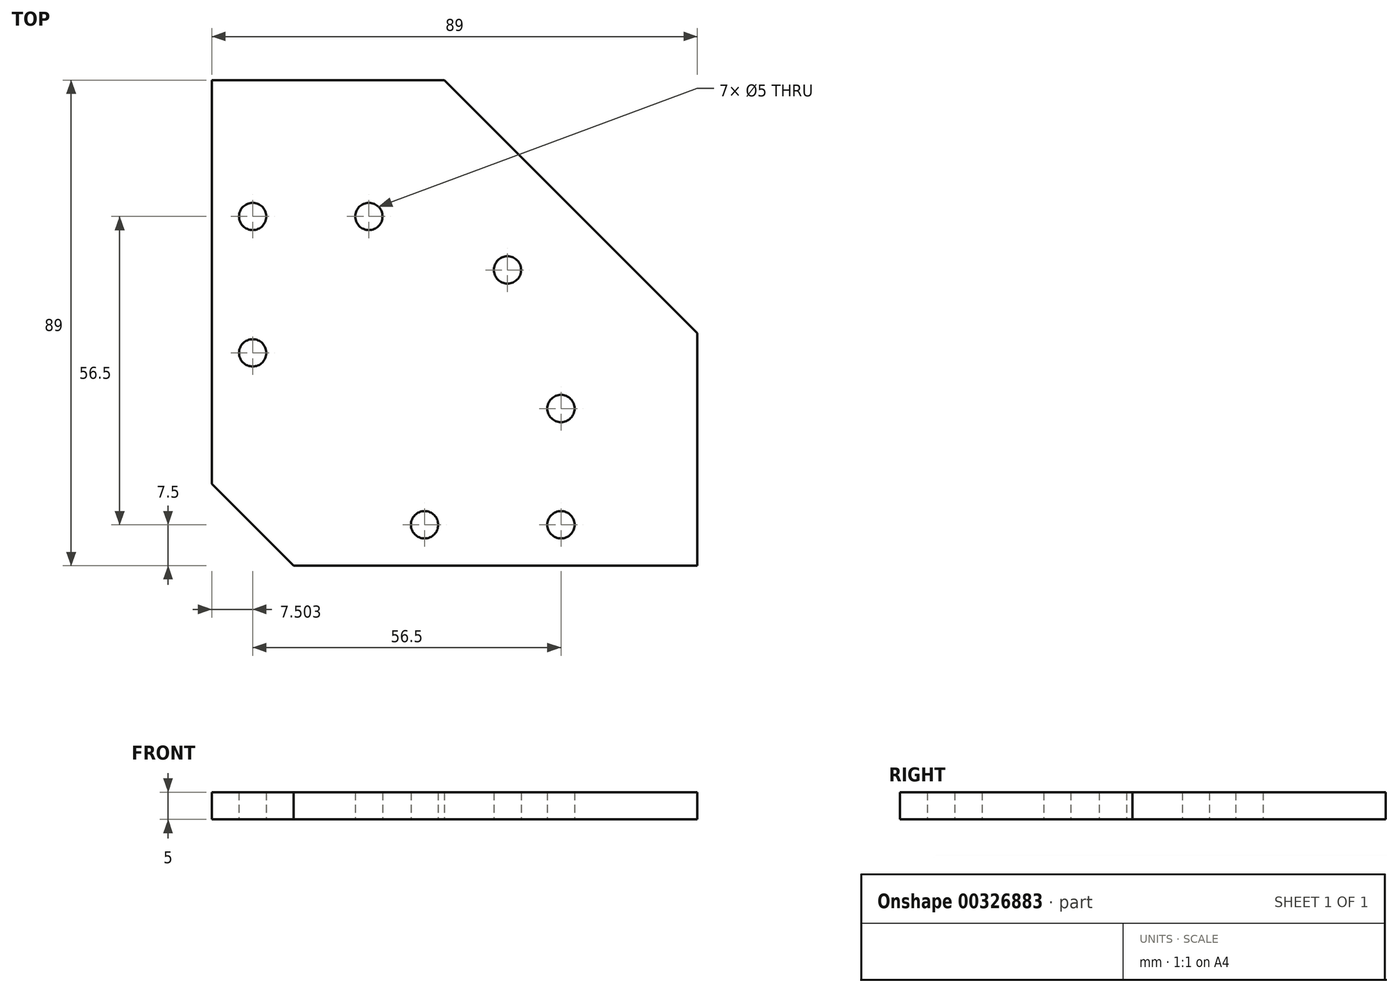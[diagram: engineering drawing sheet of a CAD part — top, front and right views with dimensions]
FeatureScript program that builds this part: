
annotation { "Feature Type Name" : "Feature", "Feature Type Description" : "" }
export const myFeature = defineFeature(function(context is Context, id is Id, definition is map)
    precondition{}
    {
        {
            var Q0;
            Q0=qCreatedBy(makeId("Top.planeOp"),FACE);
            var sketch = newSketch(context, id + "F0", { "sketchPlane" : qUnion([Q0])});
            skLineSegment(sketch, "E0.top", {"start": v(-31.5, -39.53) * mm, "end": v(42.5, -39.53) * mm});
            skLineSegment(sketch, "E1", {"start": v(-3.9, 49.47) * mm, "end": v(42.5, 3.07) * mm});
            skCircle(sketch, "E2", {"center": v(7.7, 14.67) * mm, "radius": 2.5 * mm});
            skCircle(sketch, "E3", {"center": v(-7.5, -32.03) * mm, "radius": 2.5 * mm});
            skCircle(sketch, "E4", {"center": v(-39, 24.47) * mm, "radius": 2.5 * mm});
            skCircle(sketch, "E5", {"center": v(17.5, -32.03) * mm, "radius": 2.5 * mm});
            skCircle(sketch, "E6", {"center": v(-39, -0.53) * mm, "radius": 2.5 * mm});
            skLineSegment(sketch, "E7", {"start": v(-46.5, -24.53) * mm, "end": v(-31.5, -39.53) * mm});
            skCircle(sketch, "E8", {"center": v(17.5, -10.73) * mm, "radius": 2.5 * mm});
            skCircle(sketch, "E9", {"center": v(-17.7, 24.47) * mm, "radius": 2.5 * mm});
            skLineSegment(sketch, "E10", {"start": v(-46.5, 49.47) * mm, "end": v(-3.9, 49.47) * mm});
            skLineSegment(sketch, "E11", {"start": v(-46.5, -24.53) * mm, "end": v(-46.5, 49.47) * mm});
            skLineSegment(sketch, "E12", {"start": v(42.5, 3.07) * mm, "end": v(42.5, -39.53) * mm});
            skSolve(sketch);
        }
        {
            var Q0;
            {var subQ3=sQuery(id+"F0.wireOp",EDGE,"12f35d2b-c68b-418b-b00d-b67ad5024e13.top");Q0=makeQuery(id+"F0.imprint","IMPRINT",FACE,{"disambiguationData":[TD([[makeQuery(id+"F0.imprint","IMPRINT",EDGE,{"derivedFrom":subQ3}),1.0]])]});}
            var Q1;
            {var subQ0=sQuery(id+"F0.wireOp",EDGE,"ad282f71-38ca-4f8b-a1f7-5431a2a2335f");Q1=makeQuery(id+"F0.imprint","IMPRINT",FACE,{"disambiguationData":[TD([[makeQuery(id+"F0.imprint","IMPRINT",EDGE,{"derivedFrom":subQ0}),1.0]])]});}
            var Q2;
            {var subQ0=sQuery(id+"F0.wireOp",EDGE,"38b735bb-8094-45c9-8232-a95707301399");Q2=makeQuery(id+"F0.imprint","IMPRINT",FACE,{"disambiguationData":[TD([[makeQuery(id+"F0.imprint","IMPRINT",EDGE,{"derivedFrom":subQ0}),-1.0]])]});}
            var Q3;
            Q3=makeQuery(id+"F0.imprint","IMPRINT",FACE,{"disambiguationData":[TD([[makeQuery(id+"F0.imprint","IMPRINT",EDGE,{"derivedFrom":sQuery(id+"F0.wireOp",EDGE,"5da66f6c-2266-4f65-b765-c954a388485b.left")}),1.0]])]});
            var Q4;
            {var subQ0=sQuery(id+"F0.wireOp",EDGE,"f071d871-9daf-4b47-b454-695898dbd740");Q4=makeQuery(id+"F0.imprint","IMPRINT",FACE,{"disambiguationData":[TD([[makeQuery(id+"F0.imprint","IMPRINT",EDGE,{"derivedFrom":subQ0}),-1.0]])]});}
            var Q5;
            {var subQ0=sQuery(id+"F0.wireOp",EDGE,"eb1fe70f-2a95-49aa-ad7d-cf3545569c1e.bottom");Q5=makeQuery(id+"F0.imprint","IMPRINT",FACE,{"disambiguationData":[TD([[makeQuery(id+"F0.imprint","IMPRINT",EDGE,{"derivedFrom":subQ0}),-1.0]])]});}
            var Q6;
            {var subQ0=sQuery(id+"F0.wireOp",EDGE,"f0009805-fc91-4ad8-92b9-82d7bf72914f");Q6=makeQuery(id+"F0.imprint","IMPRINT",FACE,{"disambiguationData":[TD([[makeQuery(id+"F0.imprint","IMPRINT",EDGE,{"derivedFrom":subQ0}),-1.0]])]});}
            var Q7;
            {var subQ0=sQuery(id+"F0.wireOp",EDGE,"ad282f71-38ca-4f8b-a1f7-5431a2a2335f");Q7=makeQuery(id+"F0.imprint","IMPRINT",FACE,{"disambiguationData":[TD([[makeQuery(id+"F0.imprint","IMPRINT",EDGE,{"derivedFrom":subQ0}),-1.0]])]});}
            var Q8;
            {var subQ0=sQuery(id+"F0.wireOp",EDGE,"25b59421-fc7d-4606-8aef-ece077d51384.left");Q8=makeQuery(id+"F0.imprint","IMPRINT",FACE,{"disambiguationData":[TD([[makeQuery(id+"F0.imprint","IMPRINT",EDGE,{"derivedFrom":subQ0}),-1.0]])]});}
            var Q9;
            Q9=makeQuery(id+"F0.imprint","IMPRINT",FACE,{"disambiguationData":[TD([[makeQuery(id+"F0.imprint","IMPRINT",EDGE,{"derivedFrom":sQuery(id+"F0.wireOp",EDGE,"12f35d2b-c68b-418b-b00d-b67ad5024e13.top")}),-1.0]])]});
            var Q10;
            {var subQ1=sQuery(id+"F0.wireOp",EDGE,"016ea257-698d-4f85-98c1-52bb9f978d48.bottom");var subQ3=sQuery(id+"F0.wireOp",EDGE,"a76027e1-ae81-4149-b1a1-57b07a19dd7e");var subQ4=makeQuery(id+"F0.imprint","INTERSECT",VERTEX,{"derivedFrom":[subQ1,subQ3]});Q10=makeQuery(id+"F0.imprint","IMPRINT",FACE,{"disambiguationData":[TD([[makeQuery(id+"F0.imprint","IMPRINT",EDGE,{"disambiguationData":[TD([[subQ4,1.0]])],"derivedFrom":subQ3}),-1.0]])]});}
            var Q11;
            Q11=makeQuery(id+"F0.imprint","IMPRINT",FACE,{"disambiguationData":[TD([[makeQuery(id+"F0.imprint","IMPRINT",EDGE,{"derivedFrom":sQuery(id+"F0.wireOp",EDGE,"079c5ebb-78bb-447d-bfdc-5d0deedcc594.right")}),-1.0]])]});
            var Q12;
            Q12=makeQuery(id+"F0.imprint","IMPRINT",FACE,{"disambiguationData":[TD([[makeQuery(id+"F0.imprint","IMPRINT",EDGE,{"derivedFrom":sQuery(id+"F0.wireOp",EDGE,"c6011ef3-1792-48c6-b45d-8d3b5fd57b01.top")}),-1.0]])]});
            var Q13;
            Q13=makeQuery(id+"F0.imprint","IMPRINT",FACE,{"disambiguationData":[TD([[makeQuery(id+"F0.imprint","IMPRINT",EDGE,{"derivedFrom":sQuery(id+"F0.wireOp",EDGE,"fcbf8822-de2d-44dd-b53b-8108490e90f4.bottom")}),-1.0]])]});
            var Q14;
            Q14=makeQuery(id+"F0.imprint","IMPRINT",FACE,{"disambiguationData":[TD([[makeQuery(id+"F0.imprint","IMPRINT",EDGE,{"derivedFrom":sQuery(id+"F0.wireOp",EDGE,"fcbf8822-de2d-44dd-b53b-8108490e90f4.bottom")}),1.0]])]});
            var Q15;
            Q15=makeQuery(id+"F0.imprint","IMPRINT",FACE,{"disambiguationData":[TD([[makeQuery(id+"F0.imprint","IMPRINT",EDGE,{"derivedFrom":sQuery(id+"F0.wireOp",EDGE,"cb7442d3-4b5a-4c75-a952-eb404587b997.bottom")}),-1.0]])]});
            var Q16;
            {var subQ0=sQuery(id+"F0.wireOp",EDGE,"889d1c12-67dc-48e1-96e4-abb14e17cea4.bottom");Q16=makeQuery(id+"F0.imprint","IMPRINT",FACE,{"disambiguationData":[TD([[makeQuery(id+"F0.imprint","IMPRINT",EDGE,{"derivedFrom":subQ0}),1.0]])]});}
            var Q17;
            {var subQ0=sQuery(id+"F0.wireOp",EDGE,"f2c459e5-36c8-4b73-806d-bac305cfcd8e.bottom");Q17=makeQuery(id+"F0.imprint","IMPRINT",FACE,{"disambiguationData":[TD([[makeQuery(id+"F0.imprint","IMPRINT",EDGE,{"derivedFrom":subQ0}),1.0]])]});}
            var Q18;
            Q18=makeQuery(id+"F0.imprint","IMPRINT",FACE,{"disambiguationData":[TD([[makeQuery(id+"F0.imprint","IMPRINT",EDGE,{"derivedFrom":sQuery(id+"F0.wireOp",EDGE,"079c5ebb-78bb-447d-bfdc-5d0deedcc594.right")}),1.0]])]});
            var Q19;
            {var subQ7=sQuery(id+"F0.wireOp",EDGE,"f0009805-fc91-4ad8-92b9-82d7bf72914f");Q19=makeQuery(id+"F0.imprint","IMPRINT",FACE,{"disambiguationData":[TD([[makeQuery(id+"F0.imprint","IMPRINT",EDGE,{"derivedFrom":subQ7}),1.0]])]});}
            var Q20;
            Q20=makeQuery(id+"F0.imprint","IMPRINT",FACE,{"disambiguationData":[TD([[makeQuery(id+"F0.imprint","IMPRINT",EDGE,{"derivedFrom":sQuery(id+"F0.wireOp",EDGE,"a82d30b5-7692-4b8e-9290-b3de14114a9f.top")}),1.0]])]});
            var Q21;
            Q21=makeQuery(id+"F0.imprint","IMPRINT",FACE,{"disambiguationData":[TD([[makeQuery(id+"F0.imprint","IMPRINT",EDGE,{"derivedFrom":sQuery(id+"F0.wireOp",EDGE,"421f48e6-1697-42de-85c6-57e21ccd456e.bottom")}),1.0]])]});
            var Q22;
            {var subQ4=sQuery(id+"F0.wireOp",EDGE,"E0.top");Q22=makeQuery(id+"F0.imprint","IMPRINT",FACE,{"disambiguationData":[TD([[makeQuery(id+"F0.imprint","IMPRINT",EDGE,{"derivedFrom":subQ4}),1.0]])]});}
            var Q23;
            Q23=makeQuery(id+"F0.imprint","IMPRINT",FACE,{"disambiguationData":[TD([[makeQuery(id+"F0.imprint","IMPRINT",EDGE,{"derivedFrom":sQuery(id+"F0.wireOp",EDGE,"cdae753b-1cb9-43e1-b05c-2ac3b60586a2.bottom")}),-1.0]])]});
            var Q24;
            {var subQ0=sQuery(id+"F0.wireOp",EDGE,"889d1c12-67dc-48e1-96e4-abb14e17cea4.top");Q24=makeQuery(id+"F0.imprint","IMPRINT",FACE,{"disambiguationData":[TD([[makeQuery(id+"F0.imprint","IMPRINT",EDGE,{"derivedFrom":subQ0}),-1.0]])]});}
            var Q25;
            {var subQ4=sQuery(id+"F0.wireOp",EDGE,"016ea257-698d-4f85-98c1-52bb9f978d48.right");Q25=makeQuery(id+"F0.imprint","IMPRINT",FACE,{"disambiguationData":[TD([[makeQuery(id+"F0.imprint","IMPRINT",EDGE,{"derivedFrom":subQ4}),1.0]])]});}
            var Q26;
            Q26=makeQuery(id+"F0.imprint","IMPRINT",FACE,{"disambiguationData":[TD([[makeQuery(id+"F0.imprint","IMPRINT",EDGE,{"derivedFrom":sQuery(id+"F0.wireOp",EDGE,"421f48e6-1697-42de-85c6-57e21ccd456e.bottom")}),-1.0]])]});
            var Q27;
            Q27=makeQuery(id+"F0.imprint","IMPRINT",FACE,{"disambiguationData":[TD([[makeQuery(id+"F0.imprint","IMPRINT",EDGE,{"derivedFrom":sQuery(id+"F0.wireOp",EDGE,"2debd46d-b504-47a0-ab97-af8f12a55056.bottom")}),-1.0]])]});
            extrude(context, id + "F1", {"entities" : qUnion([Q0, Q1, Q2, Q3, Q4, Q5, Q6, Q7, Q8, Q9, Q10, Q11, Q12, Q13, Q14, Q15, Q16, Q17, Q18, Q19, Q20, Q21, Q22, Q23, Q24, Q25, Q26, Q27]), "depth" : 5 * mm, "offsetDistance" : 25 * mm});
        }
    });
